# Revit family: Building-IEC309Connections-GEWISS-67IB-INTERLOCKED-SOCKET-OUTLETS_IP67_WITHOUT_BOTTOM_63A_FUS
name_source: partatom
category: Apparecchi elettrici
units: mm (PartAtom-declared; Revit-internal decimal feet)

## family parameters
Condiviso = Sì
Host = Superficie
Mantenere orientamento annotazione = Sì
Punto di calcolo locali = Sì
Quota connettore circolare = Usa diametro
Taglio con vuoti quando caricato = Sì
Tipo di parte = Normale

## types (11) — shared parameters
Catalogue = BUILDING
Catalogue Range = 67 IB
Corpo presa = GEWISS -BLU
Electrocod = 2222
Frequency = 50/60 Hz
Fuse breacking capacity = > 50 kA
Glow Wire Test = 850 °C
Glow wire test: = 850 °C
IDF = 17539d88-40d3-4220-808a-0c55cd6dcccb
IDT = 4db8474b-84e3-4347-92c1-42259bd8bc9a
IP degree = IP67
Immagine tipo = H.jpg
Operating temperature: = -25 +40 °C
Produttore = GEWISS S.p.A.
Prospetto di default = 1219 mm
Protection = Fuse-holder base (CBF)
Rated current (A) = 63
Rated current (In) = 63
Rated frequency (Hz) = 50/60 Hz
Rated impulse withstand voltage = 4KV
Rated insulation voltage (Ui) = 500V
Rated short-circuit current (Icc) = 10KA
SEO = Socket outlet
Shock resistance = IK08
Simbolo presa = PRESAINDSTAGNA : 3P
Struttura = Grigio RAL - 7035
Technical sheet = https://www.gewiss.com
Thermo-pressure with ball = 125
Type of fuse = Ã˜ 22x58 mm
Typology = Vertical
URL = https://www.gewiss.com
Version file RFA = 21.4
Weight = Max. 2.2 Kg
Weight (kg) = Max. 2.2 Kg
With back-mounting box = No
Working temperature = -25 ÷ +40 °C
presa = rosso
zero-valued in all types: giallo

## per-type parameters (varying)
| type | Colour | Colour: | Descrizione | EAN code | IB socket outlet rated current (In) | Modello | No. of poles | Number of poles | Rated voltage | Rated voltage: | Reference h |
| GW66355N - 63A 3P+N+E 500V V.INT.SOCK.O.N.B.7H CBF | Black | Black | 63A 3P+N+E 500V V.INT.SOCK.O.N.B.7H CBF | 8011564742109 | 48A | GW66355N | 3P+N+E | 3P+N+E | 480 - 500 V | 480 - 500 V | 7 |
| GW66351N - 63A 2P+E 400V V.INT.SOCK.O.N.B.6H CBF | Red | Red | 63A 2P+E 400V V.INT.SOCK.O.N.B.6H CBF | 8011564742062 | 54A | GW66351N | 2P+E | 2P+E | 380 - 415 V | 380 - 415 V | 9 |
| GW66346N - 63A 3P+E 110V V.INT.SOCK.O.N.B.4H CBF | Yellow | Yellow | 63A 3P+E 110V V.INT.SOCK.O.N.B.4H CBF | 8011564742017 | 52A | GW66346N | 3P+E | 3P+E | 100 - 130 V | 100 - 130 V | 4 |
| GW66348N - 63A 2P+E 230V V.INT.SOCK.O.N.B.6H CBF | Blue | Blue | 63A 2P+E 230V V.INT.SOCK.O.N.B.6H CBF | 8011564742031 | 54A | GW66348N | 2P+E | 2P+E | 200 - 250 V | 200 - 250 V | 6 |
| GW66354N - 63A 3P+E 500V V.INT.SOCK.O.N.B.7H CBF | Black | Black | 63A 3P+E 500V V.INT.SOCK.O.N.B.7H CBF | 8011564742093 | 52A | GW66354N | 3P+E | 3P+E | 480 - 500 V | 480 - 500 V | 7 |
| GW66352N - 63A 3P+E 400V V.INT.SOCK.O.N.B.9H CBF | Red | Red | 63A 3P+E 400V V.INT.SOCK.O.N.B.9H CBF | 8011564742079 | 52A | GW66352N | 3P+E | 3P+E | 380 - 415 V | 380 - 415 V | 6 |
| GW66350N - 63A 3P+N+E 230V V.INT.SOCK.O.N.B.9H CBF | Blue | Blue | 63A 3P+N+E 230V V.INT.SOCK.O.N.B.9H CBF | 8011564742055 | 48A | GW66350N | 3P+N+E | 3P+N+E | 200 - 250 V | 200 - 250 V | 9 |
| GW66353N - 63A 3P+N+E 400V V.INT.SOCK.O.N.B.9H CBF | Red | Red | 63A 3P+N+E 400V V.INT.SOCK.O.N.B.9H CBF | 8011564742086 | 48A | GW66353N | 3P+N+E | 3P+N+E | 380 - 415 V | 380 - 415 V | 6 |
| GW66345N - 63A 2P+E 110V V.INT.SOCK.O.N.B.4H CBF | Yellow | Yellow | 63A 2P+E 110V V.INT.SOCK.O.N.B.4H CBF | 8011564742000 | 54A | GW66345N | 2P+E | 2P+E | 100 - 130 V | 100 - 130 V | 4 |
| GW66347N - 63A 3P+N+E 110V V.INT.SOCK.O.N.B.4H CBF | Yellow | Yellow | 63A 3P+N+E 110V V.INT.SOCK.O.N.B.4H CBF | 8011564742024 | 48A | GW66347N | 3P+N+E | 3P+N+E | 100 - 130 V | 100 - 130 V | 4 |
| GW66349N - 63A 3P+E 230V V.INT.SOCK.O.N.B.9H CBF | Blue | Blue | 63A 3P+E 230V V.INT.SOCK.O.N.B.9H CBF | 8011564742048 | 52A | GW66349N | 3P+E | 3P+E | 200 - 250 V | 200 - 250 V | 9 |

note: source unit labels omitted for Thermo-pressure with ball — the stored unit's dimension contradicts the parameter name (converter mislabeling)

## geometry (parser evidence)
native form markers: Sweep x5
no freeform markers — native parametric forms only
